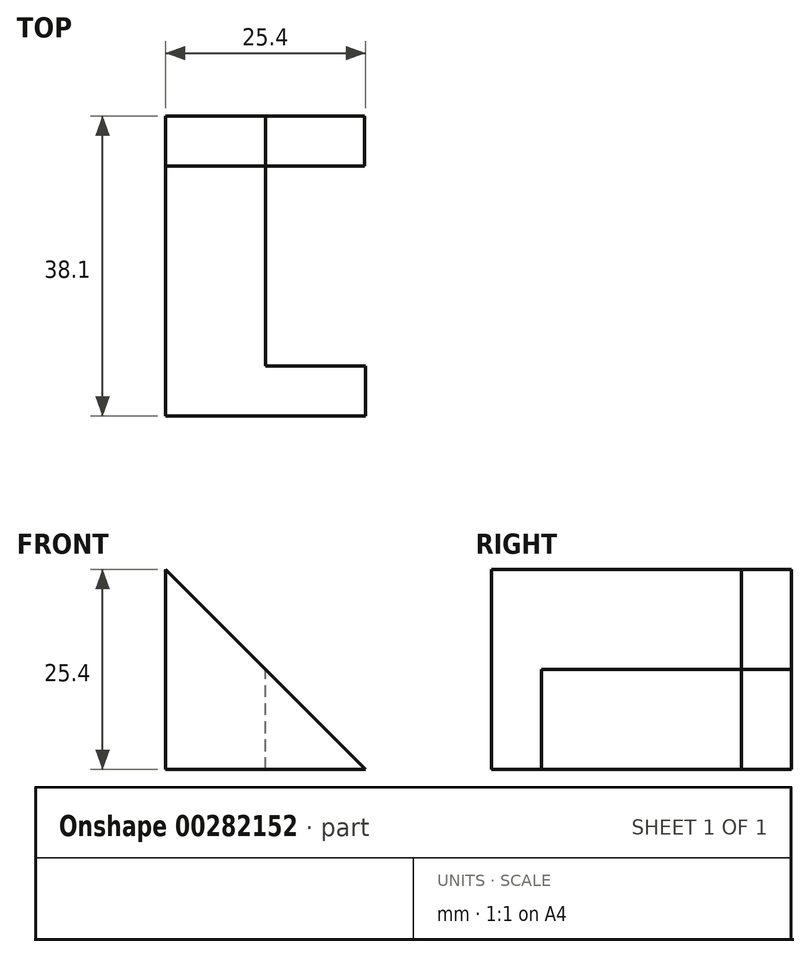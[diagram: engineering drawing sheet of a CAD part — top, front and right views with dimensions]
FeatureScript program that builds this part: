
annotation { "Feature Type Name" : "Feature", "Feature Type Description" : "" }
export const myFeature = defineFeature(function(context is Context, id is Id, definition is map)
    precondition{}
    {
        {
            var Q0;
            Q0=qCreatedBy(makeId("Front.planeOp"),FACE);
            var sketch = newSketch(context, id + "F0", { "sketchPlane" : qUnion([Q0])});
            skLineSegment(sketch, "E0", {"start": v(0, 0) * mm, "end": v(25.4, 0) * mm});
            skLineSegment(sketch, "E1", {"start": v(0, 0) * mm, "end": v(0, 25.4) * mm});
            skLineSegment(sketch, "E2", {"start": v(0, 25.4) * mm, "end": v(25.4, 0) * mm});
            skSolve(sketch);
        }
        {
            var Q0;
            Q0=makeQuery(id+"F0.imprint","IMPRINT",FACE,{"disambiguationData":[TD([[makeQuery(id+"F0.imprint","IMPRINT",EDGE,{"derivedFrom":sQuery(id+"F0.wireOp",EDGE,"E0")}),1.0]])]});
            extrude(context, id + "F1", {"entities" : qUnion([Q0]), "oppositeDirection" : true, "depth" : 6.35 * mm});
        }
        {
            var Q0;
            Q0=makeQuery(id+"F1.opExtrude","SWEPT_FACE",FACE,{"disambiguationData":[OSD([sQuery(id+"F0.wireOp",EDGE,"E1")])]});
            var sketch = newSketch(context, id + "F2", { "sketchPlane" : qUnion([Q0])});
            skLineSegment(sketch, "E3", {"start": v(-31.75, 0) * mm, "end": v(-31.75, 12.7) * mm});
            skLineSegment(sketch, "E4", {"start": v(-31.75, 0) * mm, "end": v(-6.35, 0) * mm});
            skLineSegment(sketch, "E5", {"start": v(-31.75, 12.7) * mm, "end": v(-6.35, 12.7) * mm});
            skLineSegment(sketch, "E6", {"start": v(-6.35, 12.7) * mm, "end": v(-6.35, 0) * mm});
            skSolve(sketch);
        }
        {
            var Q0;
            Q0=makeQuery(id+"F2.imprint","IMPRINT",FACE,{"disambiguationData":[TD([[makeQuery(id+"F2.imprint","IMPRINT",EDGE,{"derivedFrom":sQuery(id+"F2.wireOp",EDGE,"E3")}),-1.0]])]});
            extrude(context, id + "F3", {"entities" : qUnion([Q0]), "operationType" : NewBodyOperationType.ADD, "oppositeDirection" : true, "depth" : 12.7 * mm});
        }
        {
            var Q0;
            Q0=makeQuery(id+"F3.opExtrude","SWEPT_FACE",FACE,{"disambiguationData":[OSD([sQuery(id+"F2.wireOp",EDGE,"E3")])]});
            var sketch = newSketch(context, id + "F4", { "sketchPlane" : qUnion([Q0])});
            skLineSegment(sketch, "E7", {"start": v(0, 12.7) * mm, "end": v(0, 25.4) * mm});
            skLineSegment(sketch, "E8", {"start": v(0, 25.4) * mm, "end": v(-12.7, 12.7) * mm});
            skLineSegment(sketch, "E9", {"start": v(-12.7, 12.7) * mm, "end": v(0, 12.7) * mm});
            skSolve(sketch);
        }
        {
            var Q0;
            Q0=makeQuery(id+"F4.imprint","IMPRINT",FACE,{"disambiguationData":[TD([[makeQuery(id+"F4.imprint","IMPRINT",EDGE,{"derivedFrom":sQuery(id+"F4.wireOp",EDGE,"E7")}),1.0]])]});
            extrude(context, id + "F5", {"entities" : qUnion([Q0]), "operationType" : NewBodyOperationType.ADD, "oppositeDirection" : true, "depth" : 25.4 * mm});
        }
        {
            var Q0;
            Q0=makeQuery(id+"F5.boolean.opBoolean","MERGE",FACE,{"derivedFrom":[makeQuery(id+"F3.opExtrude","SWEPT_FACE",FACE,{"disambiguationData":[OSD([sQuery(id+"F2.wireOp",EDGE,"E3")])]}),makeQuery(id+"F5.opExtrude","CAP_FACE",FACE,{"disambiguationData":[OSD([sQuery(id+"F4.wireOp",EDGE,"E7"),sQuery(id+"F4.wireOp",EDGE,"E8"),sQuery(id+"F4.wireOp",EDGE,"E9")])],"isStart":true})]});
            var sketch = newSketch(context, id + "F6", { "sketchPlane" : qUnion([Q0])});
            skLineSegment(sketch, "E10", {"start": v(-12.7, 0) * mm, "end": v(-25.28, 0) * mm});
            skLineSegment(sketch, "E11", {"start": v(-12.7, 0) * mm, "end": v(-12.7, 12.7) * mm});
            skLineSegment(sketch, "E12", {"start": v(-12.7, 12.7) * mm, "end": v(-25.28, 0) * mm});
            skSolve(sketch);
        }
        {
            var Q0;
            Q0=makeQuery(id+"F6.imprint","IMPRINT",FACE,{"disambiguationData":[TD([[makeQuery(id+"F6.imprint","IMPRINT",EDGE,{"derivedFrom":sQuery(id+"F6.wireOp",EDGE,"E10")}),-1.0]])]});
            extrude(context, id + "F7", {"entities" : qUnion([Q0]), "depth" : 6.35 * mm});
        }
        {
            var Q0;
            Q0=makeQuery(id+"F7.opExtrude","CAP_FACE",FACE,{"disambiguationData":[OSD([sQuery(id+"F6.wireOp",EDGE,"E10"),sQuery(id+"F6.wireOp",EDGE,"E11"),sQuery(id+"F6.wireOp",EDGE,"E12")])],"isStart":false});
            var sketch = newSketch(context, id + "F8", { "sketchPlane" : qUnion([Q0])});
            skLineSegment(sketch, "E13", {"start": v(-12.7, 12.7) * mm, "end": v(0, 25.4) * mm});
            skLineSegment(sketch, "E14", {"start": v(0, 25.4) * mm, "end": v(0, 0) * mm});
            skLineSegment(sketch, "E15", {"start": v(0, 0) * mm, "end": v(-12.7, 0) * mm});
            skLineSegment(sketch, "E16", {"start": v(-12.7, 0) * mm, "end": v(-12.7, 12.7) * mm});
            skSolve(sketch);
        }
        {
            var Q0;
            Q0 = qSketchRegion(id + "F8", true);
            extrude(context, id + "F9", {"entities" : qUnion([Q0]), "oppositeDirection" : true, "depth" : 6.35 * mm});
        }
    });
